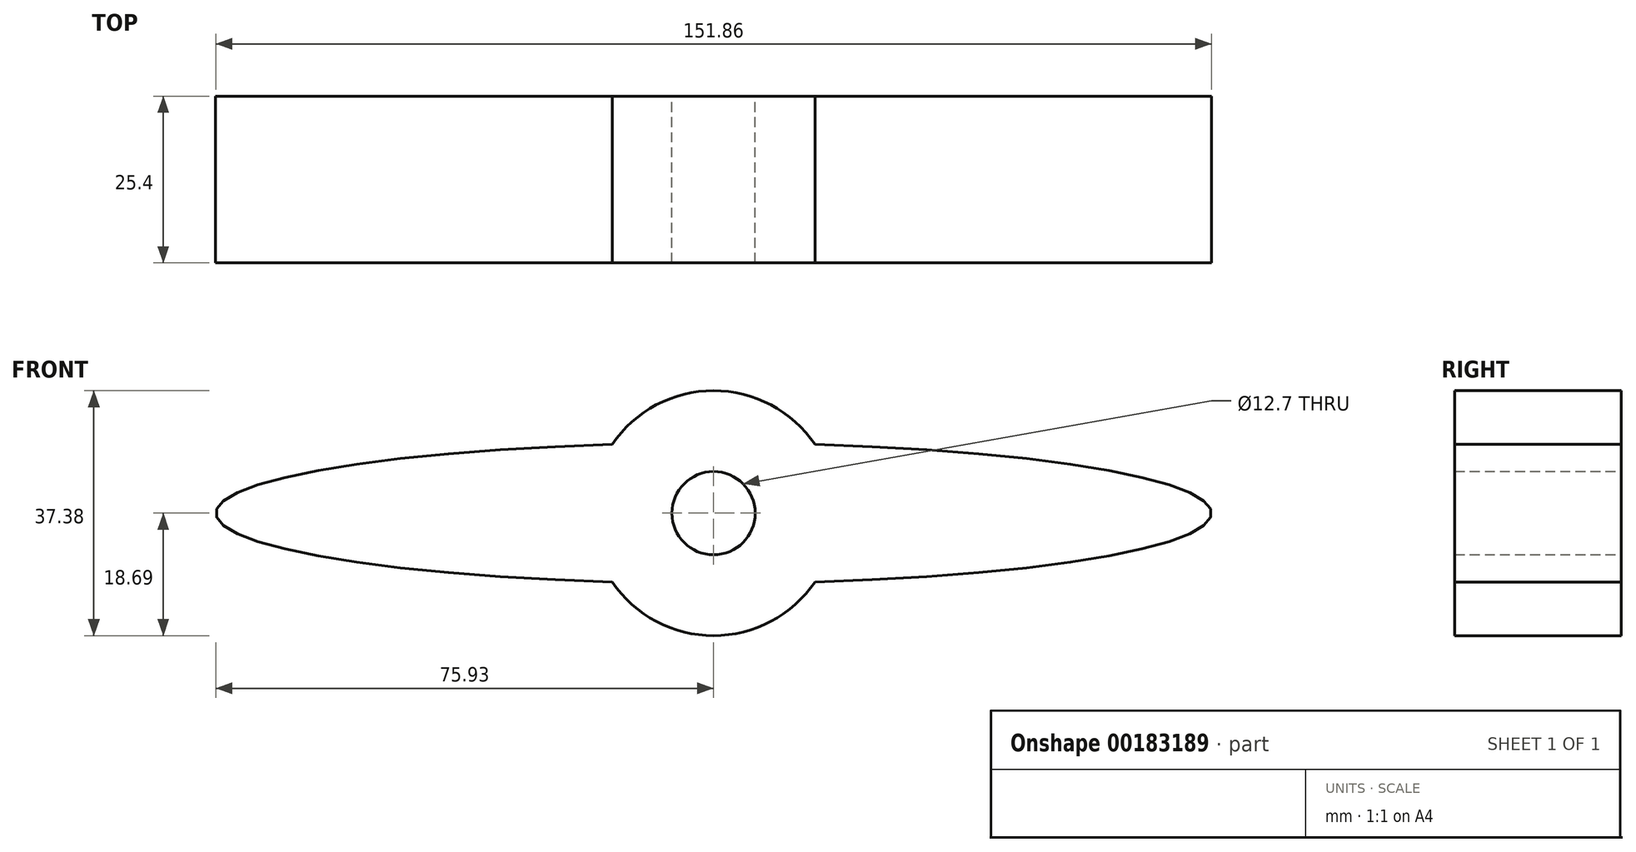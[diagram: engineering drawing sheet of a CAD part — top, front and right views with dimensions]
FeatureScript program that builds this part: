
annotation { "Feature Type Name" : "Feature", "Feature Type Description" : "" }
export const myFeature = defineFeature(function(context is Context, id is Id, definition is map)
    precondition{}
    {
        {
            var Q0;
            Q0=qCreatedBy(makeId("Front.planeOp"),FACE);
            var sketch = newSketch(context, id + "F0", { "sketchPlane" : qUnion([Q0])});
            skCircle(sketch, "E0", {"center": v(0, 0) * mm, "radius": 18.69 * mm});
            skEllipse(sketch, "E1", {"center": v(0, 0) * mm, "majorRadius": 75.93 * mm, "minorRadius": 10.71 * mm, "majorAxis": v(-1, 0)});
            skSolve(sketch);
        }
        {
            var Q0;
            Q0 = qSketchRegion(id + "F0", true);
            extrude(context, id + "F1", {"entities" : qUnion([Q0]), "depth" : 25.4 * mm});
        }
        {
            var Q0;
            Q0=sQuery(id+"F0.wireOp",VERTEX,"E0.center");
            var Q1;
            Q1=makeQuery(id+"F1.opExtrude","SWEPT_BODY",BODY,{"disambiguationData":[OSD([sQuery(id+"F0.wireOp",EDGE,"E0"),sQuery(id+"F0.wireOp",EDGE,"E1")])]});
            hole(context, id + "F2", {"style" : HoleStyle.SIMPLE, "endStyle" : HoleEndStyle.THROUGH, "oppositeDirection" : true, "holeDiameter" : 12.7 * mm, "locations" : qUnion([Q0]), "scope" : qUnion([Q1]), "isTappedThrough" : true});
        }
    });
